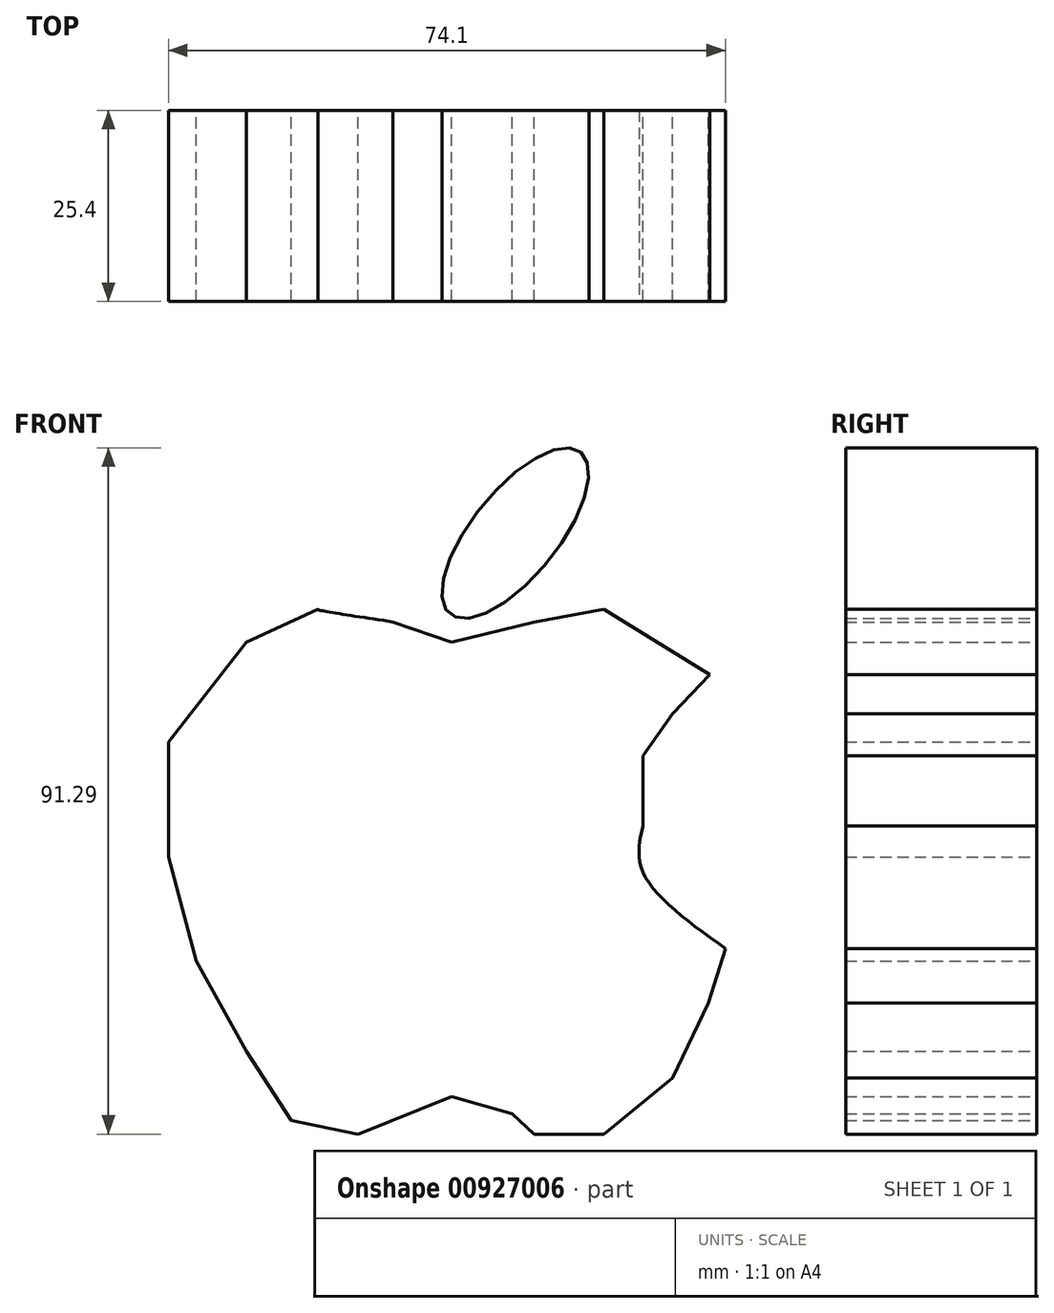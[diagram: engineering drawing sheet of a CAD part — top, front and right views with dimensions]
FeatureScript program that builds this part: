
annotation { "Feature Type Name" : "Feature", "Feature Type Description" : "" }
export const myFeature = defineFeature(function(context is Context, id is Id, definition is map)
    precondition{}
    {
        {
            var Q0;
            Q0=qCreatedBy(makeId("Front.planeOp"),FACE);
            var sketch = newSketch(context, id + "F0", { "sketchPlane" : qUnion([Q0])});
            skFitSpline(sketch, "E0", {"points": [v(42.16, 16.57) * mm, v(37.2, 11.4) * mm], "startDerivative": vector(-4.97, -5.17) * mm, "endDerivative": vector(-4.97, -5.17) * mm});
            skFitSpline(sketch, "E1", {"points": [v(37.2, 11.4) * mm, v(33.26, 5.8) * mm], "startDerivative": vector(-3.93, -5.59) * mm, "endDerivative": vector(-3.93, -5.59) * mm});
            skFitSpline(sketch, "E2", {"points": [v(33.26, -3.5) * mm, v(33.26, 5.8) * mm], "startDerivative": vector(0, 9.31) * mm, "endDerivative": vector(0, 9.31) * mm});
            skFitSpline(sketch, "E3", {"points": [v(33.26, -3.5) * mm, v(33.26, -9.71) * mm, v(44.23, -19.86) * mm], "startDerivative": vector(-3.54, -15.68) * mm, "endDerivative": vector(23.53, -16.94) * mm});
            skFitSpline(sketch, "E4", {"points": [v(44.23, -19.86) * mm, v(41.95, -27.1) * mm], "startDerivative": vector(-2.28, -7.24) * mm, "endDerivative": vector(-2.28, -7.24) * mm});
            skFitSpline(sketch, "E5", {"points": [v(41.95, -27.1) * mm, v(37.2, -37.04) * mm], "startDerivative": vector(-4.76, -9.93) * mm, "endDerivative": vector(-4.76, -9.93) * mm});
            skFitSpline(sketch, "E6", {"points": [v(37.2, -37.04) * mm, v(28.08, -44.53) * mm], "startDerivative": vector(-9.1, -7.5) * mm, "endDerivative": vector(-9.1, -7.5) * mm});
            skFitSpline(sketch, "E7", {"points": [v(28.08, -44.53) * mm, v(18.77, -44.53) * mm], "startDerivative": vector(-9.31, 0) * mm, "endDerivative": vector(-9.31, 0) * mm});
            skFitSpline(sketch, "E8", {"points": [v(18.77, -44.53) * mm, v(15.87, -41.8) * mm], "startDerivative": vector(-2.9, 2.74) * mm, "endDerivative": vector(-2.9, 2.74) * mm});
            skFitSpline(sketch, "E9", {"points": [v(15.87, -41.8) * mm, v(7.8, -39.52) * mm], "startDerivative": vector(-8.07, 2.28) * mm, "endDerivative": vector(-8.07, 2.28) * mm});
            skFitSpline(sketch, "E10", {"points": [v(7.8, -39.52) * mm, v(-4.62, -44.53) * mm], "startDerivative": vector(-12.42, -5.01) * mm, "endDerivative": vector(-12.42, -5.01) * mm});
            skFitSpline(sketch, "E11", {"points": [v(-4.62, -44.53) * mm, v(-13.52, -42.7) * mm], "startDerivative": vector(-8.9, 1.82) * mm, "endDerivative": vector(-8.9, 1.82) * mm});
            skFitSpline(sketch, "E12", {"points": [v(-13.52, -42.7) * mm, v(-19.52, -33.52) * mm], "startDerivative": vector(-6, 9.2) * mm, "endDerivative": vector(-6, 9.2) * mm});
            skFitSpline(sketch, "E13", {"points": [v(-19.52, -33.52) * mm, v(-26.14, -21.51) * mm], "startDerivative": vector(-6.62, 12) * mm, "endDerivative": vector(-6.62, 12) * mm});
            skFitSpline(sketch, "E14", {"points": [v(-26.14, -21.51) * mm, v(-29.87, -7.64) * mm], "startDerivative": vector(-3.73, 13.87) * mm, "endDerivative": vector(-3.73, 13.87) * mm});
            skFitSpline(sketch, "E15", {"points": [v(-29.87, -7.64) * mm, v(-29.87, 7.67) * mm], "startDerivative": vector(0, 15.32) * mm, "endDerivative": vector(0, 15.32) * mm});
            skFitSpline(sketch, "E16", {"points": [v(-29.87, 7.67) * mm, v(-19.52, 20.92) * mm], "startDerivative": vector(10.35, 13.25) * mm, "endDerivative": vector(10.35, 13.25) * mm});
            skFitSpline(sketch, "E17", {"points": [v(-19.52, 20.92) * mm, v(-10, 25.27) * mm], "startDerivative": vector(9.52, 4.35) * mm, "endDerivative": vector(9.52, 4.35) * mm});
            skFitSpline(sketch, "E18", {"points": [v(-8.55, 25.27) * mm, v(-10, 25.27) * mm, v(0, 23.6) * mm], "startDerivative": vector(-7.9, 0.31) * mm, "endDerivative": vector(20.7, -3.1) * mm});
            skFitSpline(sketch, "E19", {"points": [v(0, 23.6) * mm, v(7.8, 20.92) * mm], "startDerivative": vector(7.8, -2.7) * mm, "endDerivative": vector(7.8, -2.7) * mm});
            skFitSpline(sketch, "E20", {"points": [v(7.8, 20.92) * mm, v(18.77, 23.6) * mm], "startDerivative": vector(10.97, 2.7) * mm, "endDerivative": vector(10.97, 2.7) * mm});
            skFitSpline(sketch, "E21", {"points": [v(18.77, 23.6) * mm, v(28.08, 25.27) * mm], "startDerivative": vector(9.31, 1.66) * mm, "endDerivative": vector(9.31, 1.66) * mm});
            skFitSpline(sketch, "E22", {"points": [v(28.08, 25.27) * mm, v(42.16, 16.57) * mm], "startDerivative": vector(14.07, -8.7) * mm, "endDerivative": vector(14.07, -8.7) * mm});
            skEllipse(sketch, "E23", {"center": v(16.29, 35.4) * mm, "majorRadius": 13.84 * mm, "minorRadius": 5.73 * mm, "majorAxis": v(0.63, 0.78)});
            skSolve(sketch);
        }
        {
            var Q0;
            Q0 = qSketchRegion(id + "F0", true);
            extrude(context, id + "F1", {"entities" : qUnion([Q0]), "depth" : 25.4 * mm, "offsetDistance" : 25.4 * mm});
        }
    });
